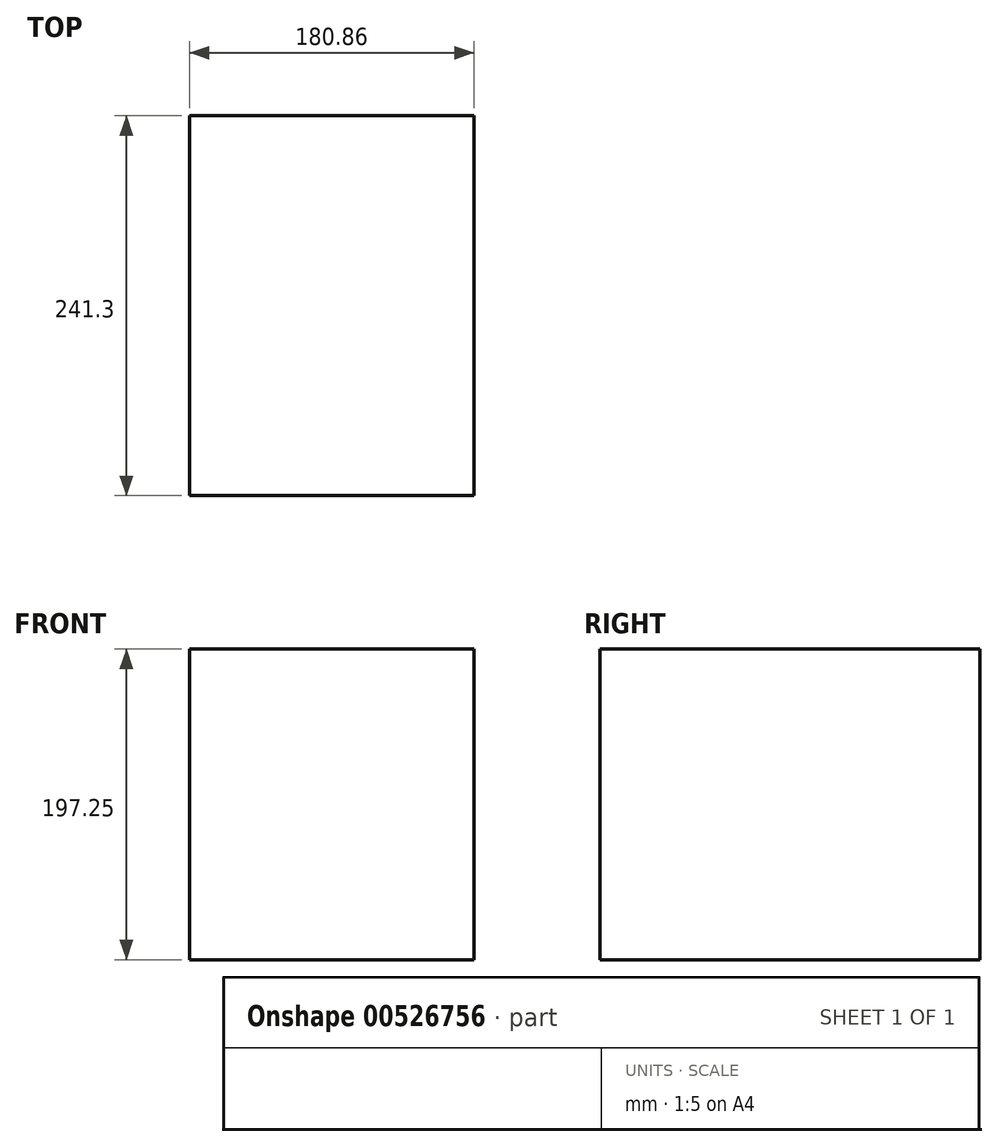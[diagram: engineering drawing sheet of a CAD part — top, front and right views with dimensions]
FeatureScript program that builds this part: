
annotation { "Feature Type Name" : "Feature", "Feature Type Description" : "" }
export const myFeature = defineFeature(function(context is Context, id is Id, definition is map)
    precondition{}
    {
        {
            var Q0;
            Q0=qCreatedBy(makeId("Front.planeOp"),FACE);
            var sketch = newSketch(context, id + "F0", { "sketchPlane" : qUnion([Q0])});
            skLineSegment(sketch, "E0.bottom", {"start": v(0, 0) * mm, "end": v(180.86, 0) * mm});
            skLineSegment(sketch, "E0.top", {"start": v(0, 197.25) * mm, "end": v(180.86, 197.25) * mm});
            skLineSegment(sketch, "E0.left", {"start": v(0, 0) * mm, "end": v(0, 197.25) * mm});
            skLineSegment(sketch, "E0.right", {"start": v(180.86, 0) * mm, "end": v(180.86, 197.25) * mm});
            skSolve(sketch);
        }
        {
            var Q0;
            Q0=makeQuery(id+"F0.imprint","IMPRINT",FACE,{"disambiguationData":[TD([[makeQuery(id+"F0.imprint","IMPRINT",EDGE,{"derivedFrom":sQuery(id+"F0.wireOp",EDGE,"E0.bottom")}),1.0]])]});
            extrude(context, id + "F1", {"entities" : qUnion([Q0]), "depth" : 241.3 * mm, "offsetDistance" : 25.4 * mm});
        }
    });
